# Revit family: Wicline_95_Glazed_in_fixed_light_composite
name_source: partatom
category: Windows
revit_build: Autodesk Revit Architecture 2014 (Build: 20130308_1515(x64)
units: mm (PartAtom-declared; Revit-internal decimal feet)

## types (1)
- Wicline_95_Glazed_in_fixed_light_composite
    Acoustic = Rw (C;Ctr) = 47 (-1;-4) dB
    Air Permeability = Class 5
    Analytic Construction = <None>
    Date of publishing = 3/14/2015
    Default Sill Height = 800 mm  [stored 2.62467 ft]
    Description = The WICLINE 95 window system meets the highest energy efficiency standards with a frame depth of only 95 mm and a slim sightline of only 125 mm. The Thermo Frame insulation zone for WICLINE 95 is located inside the rebate area of the window and can be fabricated and installed quickly and easily through an intelligent clamping system. This feature allows adjustment of the Uf-value as required for the building. The main components of the WICLINE 65 and 75 series are used for WICLINE 95 in line with the WICONA Unysis principle to simplify ordering and minimize stock keeping. The new ETC Intelligence® thermal break zone through its intelligent material mix achieves passive house class phB and removes the need for foam inserts in the sash or frame profile.
    Design country = Germany
    Edition number = 1
    Frame 1019004 = No
    Frame 1019006 = Yes
    Frame 1019010 = No
    Frame Material = WICONA - Aluminium - RAL7016 - Anthracite Grey - Matt
    Frame Thickness = 95 mm  [stored 0.31168 ft]
    Frame Width = 85 mm  [stored 0.278871 ft]
    Frame Width 2 Glass = 67 mm  [stored 0.219816 ft]
    Frame Width 3 = 82 mm  [stored 0.269029 ft]
    Frame Width 4 = 45 mm  [stored 0.147638 ft]
    Frame Width 5 Glass = 27 mm
    Frame Width 6 = 42 mm
    Glass Material = WICONA -  Glass
    Handle Material = Aluminium
    Height = 1500 mm  [stored 4.92126 ft]
    Leaf Height = 1366 mm  [stored 4.48163 ft]
    Leaf Material = WICONA - Aluminium - RAL7016 - Anthracite Grey - Matt
    Leaf Width = 1466 mm  [stored 4.80971 ft]
    Manufacturer = Wicona
    Manufacturer country = Germany
    Manufacturer name = Wicona
    Material main = Aluminium
    Material secondary = Glass
    Maximum Sash Weight = 150kg as standard design, heavier weights can easily be customised
    Mechanical Strength = Class 4
    Model = Wicline 95
    Nominal height = 150000
    Nominal width = 100000
    Operating Forces = Class 1
    Product Guid = e95bb49c-67c8-4fe8-88fb-b6bba030be1f
    Product SKU = WICLINE_95_W
    Product data url = http://bimobject.com
    Product family = Windows & Doors
    Product group = Windows
    QR code = http://bimobject.com
    Quality Assurance = Certified according to ISO 9001:2008
Certified according to ISO 9001:2008
    Repeated Opening/Closing = Class 3 (20,000 cycles)
    Resistance to wind load = Class C5/B5
    Transom 1019204 = Yes
    Transom 1019206 = No
    Transom 1019209 = No
    Transom 1019213 = No
    URL = http://www.wicona.com
    Wall Closure = By host
    Watertightness = E900
    Weight Net (Kg) = 0
    Width = 1600 mm  [stored 5.24934 ft]
    Window Offset = 60 mm  [stored 0.19685 ft]

note: [stored X ft] marks values corroborated as IEEE doubles in the binary element streams (Revit-internal decimal feet)

## geometry (parser evidence)
native form markers: Blend x4, Sweep x8
no freeform markers — native parametric forms only
